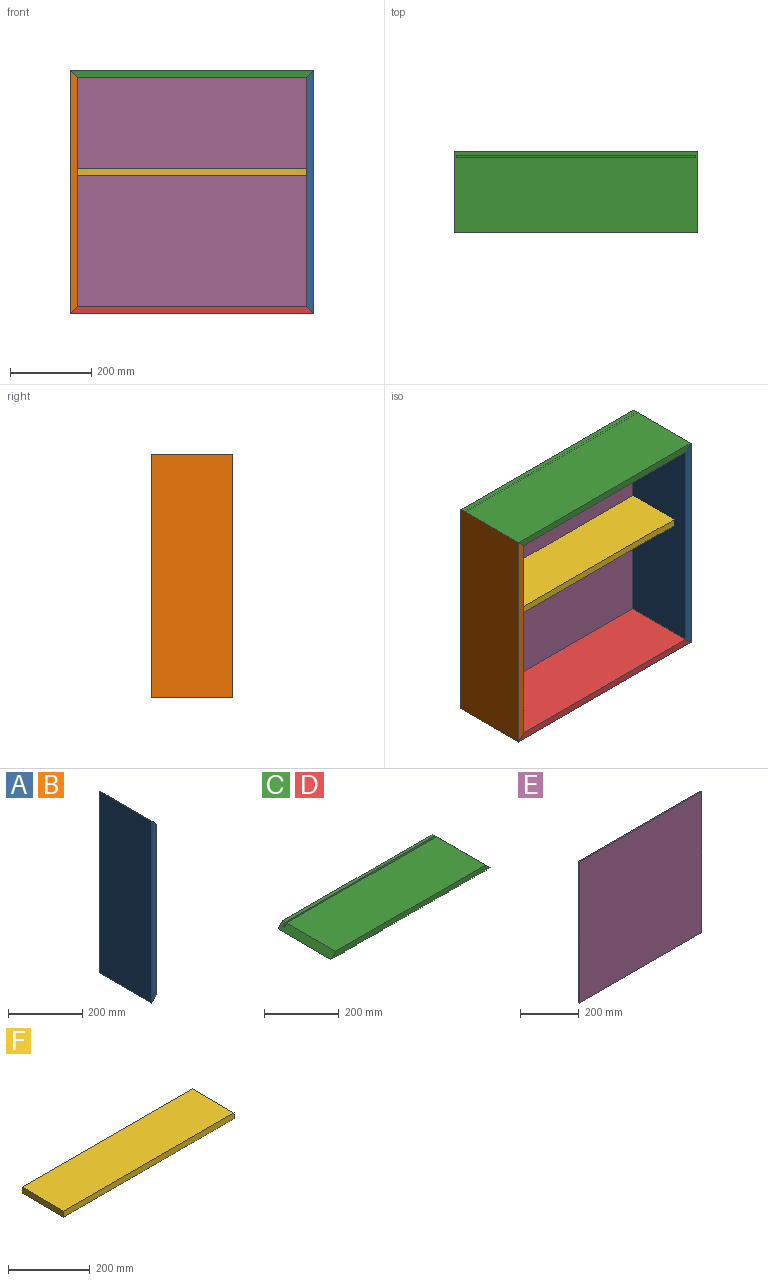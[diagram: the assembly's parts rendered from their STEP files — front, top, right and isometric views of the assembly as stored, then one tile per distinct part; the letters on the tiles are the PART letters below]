
ASSEMBLY  parts=6 mates=7
PART A: 10 faces, bbox 18x200x600 mm
  f0: plane 564x10mm, normal (1,0,0), area 5640mm2, adj f3,f6,f8,f9
  f1: plane 600x18mm, normal (0,-1,0), area 10476mm2, adj f2,f7,f8,f9
  f2: plane 564x185mm, normal (1,0,0), area 104340mm2, adj f1,f4,f8,f9
  f3: plane 600x18mm, normal (0,1,0), area 10476mm2, adj f0,f7,f8,f9
  f4: plane 584x10mm, normal (0,1,0), area 5740mm2, adj f2,f5,f8,f9
  f5: plane 584x5mm, normal (1,0,0), area 2920mm2, adj f4,f6,f8,f9
  f6: plane 584x10mm, normal (0,-1,0), area 5740mm2, adj f0,f5,f8,f9
  f7: plane 600x200mm, normal (-1,0,0), area 120000mm2, adj f1,f3,f8,f9
  f8: plane 200x18mm, normal (0.71,0,0.71), area 5020.5mm2, adj f0,f1,f2,f3,f4,f5,f6,f7
  f9: plane 200x18mm, normal (0.71,0,-0.71), area 5020.5mm2, adj f0,f1,f2,f3,f4,f5,f6,f7
PART B: same geometry as A
PART C: 10 faces, bbox 600x200x18 mm
  f0: plane 564x10mm, normal (0,0,1), area 5640mm2, adj f3,f4,f8,f9
  f1: plane 600x18mm, normal (0,-1,0), area 10476mm2, adj f2,f7,f8,f9
  f2: plane 564x185mm, normal (0,0,1), area 104340mm2, adj f1,f5,f8,f9
  f3: plane 600x18mm, normal (0,1,0), area 10476mm2, adj f0,f7,f8,f9
  f4: plane 584x10mm, normal (0,-1,0), area 5740mm2, adj f0,f6,f8,f9
  f5: plane 584x10mm, normal (0,1,0), area 5740mm2, adj f2,f6,f8,f9
  f6: plane 584x5mm, normal (0,0,1), area 2920mm2, adj f4,f5,f8,f9
  f7: plane 600x200mm, normal (0,0,-1), area 120000mm2, adj f1,f3,f8,f9
  f8: plane 200x18mm, normal (0.71,0,0.71), area 5020.5mm2, adj f0,f1,f2,f3,f4,f5,f6,f7
  f9: plane 200x18mm, normal (-0.71,0,0.71), area 5020.5mm2, adj f0,f1,f2,f3,f4,f5,f6,f7
PART D: same geometry as C
PART E: 6 faces, bbox 590x5x590 mm
  f0: plane 590x5mm, normal (0,0,1), area 2950mm2, adj f1,f3,f4,f5
  f1: plane 590x5mm, normal (-1,0,0), area 2950mm2, adj f0,f2,f4,f5
  f2: plane 590x5mm, normal (0,0,-1), area 2950mm2, adj f1,f3,f4,f5
  f3: plane 590x5mm, normal (1,0,0), area 2950mm2, adj f0,f2,f4,f5
  f4: plane 590x590mm, normal (0,-1,0), area 348100mm2, adj f0,f1,f2,f3
  f5: plane 590x590mm, normal (0,1,0), area 348100mm2, adj f0,f1,f2,f3
PART F: 6 faces, bbox 590x145x18 mm
  f0: plane 590x18mm, normal (0,1,0), area 10620mm2, adj f1,f3,f4,f5
  f1: plane 145x18mm, normal (-1,0,0), area 2610mm2, adj f0,f2,f4,f5
  f2: plane 590x18mm, normal (0,-1,0), area 10620mm2, adj f1,f3,f4,f5
  f3: plane 145x18mm, normal (1,0,0), area 2610mm2, adj f0,f2,f4,f5
  f4: plane 590x145mm, normal (0,0,1), area 85550mm2, adj f0,f1,f2,f3
  f5: plane 590x145mm, normal (0,0,-1), area 85550mm2, adj f0,f1,f2,f3
PLACE A rot(axis=(0,1,0),180deg) t=(300,-85.18,166.26)mm
PLACE B t=(-300,-85.18,-172.26)mm
PLACE C rot(axis=(0,1,0),180deg) t=(-10.49,-73.26,297)mm
PLACE D t=(10.49,-73.26,-303)mm
PLACE E t=(7.44,5,-86.19)mm
PLACE F t=(-3.59,53.75,38)mm
MATE planar F.f1 <-> E.f1  axis (-1,0,0) through (-295,-72.5,47)mm
MATE fastened A.f1 <-> D.f1  axis (0,-1,0) through (300,-185,-303)mm
MATE fastened A.f1 <-> C.f1  axis (0,-1,0) through (300,-185,297)mm
MATE planar E.f4 <-> F.f0  axis (0,-1,0) through (0,0,0)mm
MATE parallel F.f4 <-> C.f2  axis (0,0,1) through (0,-72.5,56)mm
MATE fastened C.f1 <-> B.f1  axis (0,-1,0) through (-300,-185,297)mm
MATE fastened D.f6 <-> E.f2  axis (0,0,1) through (0,2.5,-295)mm
